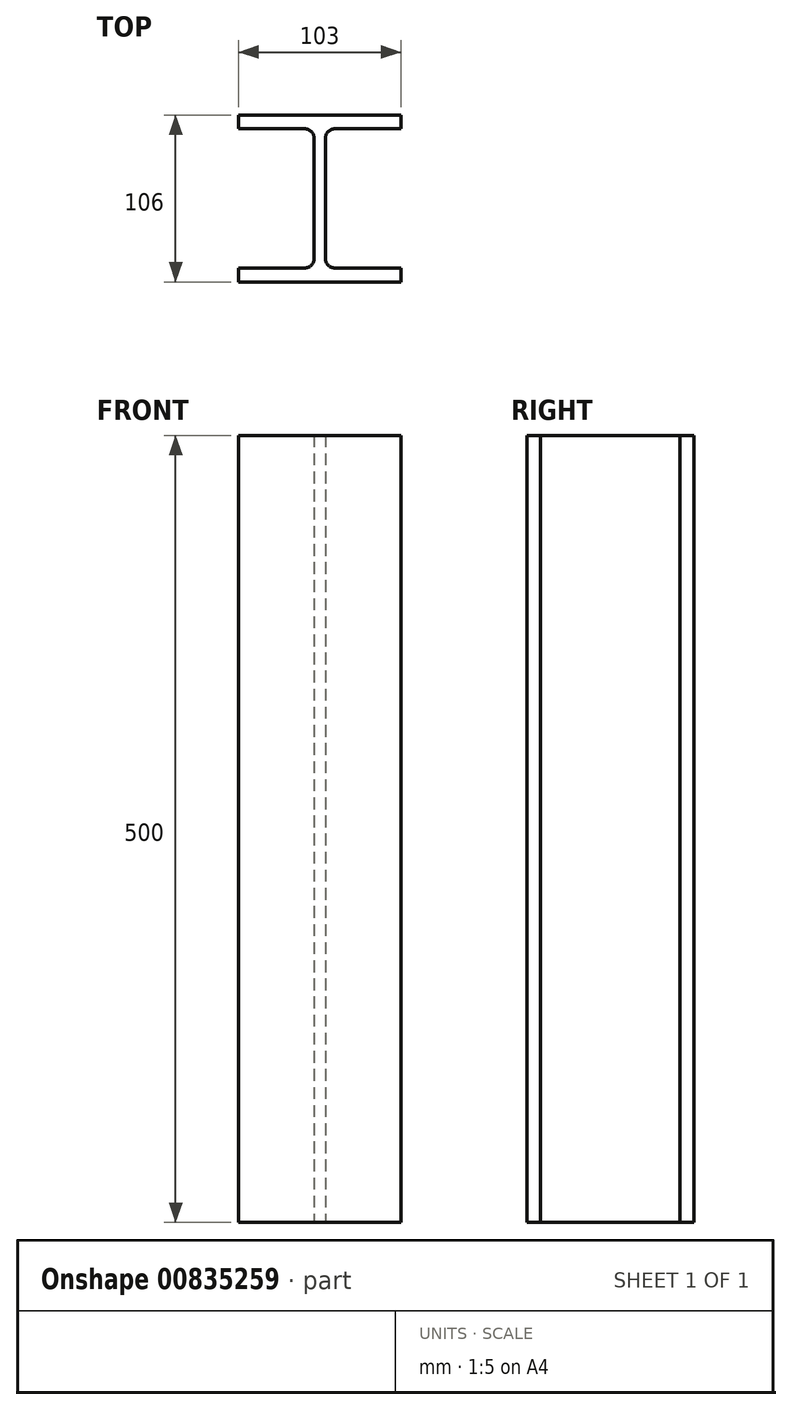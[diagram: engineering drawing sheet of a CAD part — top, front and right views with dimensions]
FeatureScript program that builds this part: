
annotation { "Feature Type Name" : "Feature", "Feature Type Description" : "" }
export const myFeature = defineFeature(function(context is Context, id is Id, definition is map)
    precondition{}
    {
        {
            var Q0;
            Q0=qCreatedBy(makeId("Top.planeOp"),FACE);
            var sketch = newSketch(context, id + "F0", { "sketchPlane" : qUnion([Q0])});
            skLineSegment(sketch, "E0.bottom", {"start": v(0, 0) * mm, "end": v(-103, 0) * mm});
            skLineSegment(sketch, "E0.top", {"start": v(0, 8.8) * mm, "end": v(-103, 8.8) * mm});
            skLineSegment(sketch, "E0.left", {"start": v(0, 0) * mm, "end": v(0, 8.8) * mm});
            skLineSegment(sketch, "E0.right", {"start": v(-103, 0) * mm, "end": v(-103, 8.8) * mm});
            skLineSegment(sketch, "E1", {"start": v(-51.5, 0) * mm, "end": v(-51.5, 106) * mm});
            skLineSegment(sketch, "E2.bottom", {"start": v(-47.95, 8.8) * mm, "end": v(-55.05, 8.8) * mm});
            skLineSegment(sketch, "E2.top", {"start": v(-47.95, 97.2) * mm, "end": v(-55.05, 97.2) * mm});
            skLineSegment(sketch, "E2.left", {"start": v(-47.95, 14.8) * mm, "end": v(-47.95, 91.2) * mm});
            skLineSegment(sketch, "E2.right", {"start": v(-55.05, 14.8) * mm, "end": v(-55.05, 91.2) * mm});
            skPoint(sketch, "E2.middle", {"position": v(-51.5, 53) * mm});
            skLineSegment(sketch, "E3", {"start": v(-51.5, 106) * mm, "end": v(0, 106) * mm});
            skLineSegment(sketch, "E4", {"start": v(0, 106) * mm, "end": v(0, 97.2) * mm});
            skLineSegment(sketch, "E5", {"start": v(0, 97.2) * mm, "end": v(-41.95, 97.2) * mm});
            skLineSegment(sketch, "E6", {"start": v(-61.05, 97.2) * mm, "end": v(-103, 97.2) * mm});
            skLineSegment(sketch, "E7", {"start": v(-103, 97.2) * mm, "end": v(-103, 106) * mm});
            skLineSegment(sketch, "E8", {"start": v(-103, 106) * mm, "end": v(-51.5, 106) * mm});
            skPoint(sketch, "E9.newPointB", {"position": v(-51.5, 97.2) * mm});
            skArc(sketch, "E9.filletArc", {"start": v(-41.95, 97.2) * mm, "mid": v(-46.2, 95.44) * mm, "end": v(-47.95, 91.2) * mm});
            skLineSegment(sketch, "E10", {"start": v(-103, 8.8) * mm, "end": v(-61.05, 8.8) * mm});
            skLineSegment(sketch, "E11", {"start": v(0, 8.8) * mm, "end": v(-41.95, 8.8) * mm});
            skPoint(sketch, "E12.visualSharp", {"position": v(-47.95, 8.8) * mm});
            skArc(sketch, "E12.filletArc", {"start": v(-47.95, 14.8) * mm, "mid": v(-46.2, 10.56) * mm, "end": v(-41.95, 8.8) * mm});
            skPoint(sketch, "E13.visualSharp", {"position": v(-55.05, 8.8) * mm});
            skArc(sketch, "E13.filletArc", {"start": v(-61.05, 8.8) * mm, "mid": v(-56.8, 10.56) * mm, "end": v(-55.05, 14.8) * mm});
            skArc(sketch, "E14.filletArc", {"start": v(-55.05, 91.2) * mm, "mid": v(-56.8, 95.44) * mm, "end": v(-61.05, 97.2) * mm});
            skSolve(sketch);
        }
        {
            var Q0;
            Q0=makeQuery(id+"F0.imprint","IMPRINT",FACE,{"disambiguationData":[TD([[makeQuery(id+"F0.imprint","IMPRINT",EDGE,{"derivedFrom":sQuery(id+"F0.wireOp",EDGE,"E2.right")}),-1.0]])]});
            var Q1;
            Q1=makeQuery(id+"F0.imprint","IMPRINT",FACE,{"disambiguationData":[TD([[makeQuery(id+"F0.imprint","IMPRINT",EDGE,{"derivedFrom":sQuery(id+"F0.wireOp",EDGE,"E2.left")}),1.0]])]});
            var Q2;
            {var subQ5=sQuery(id+"F0.wireOp",EDGE,"E0.left");Q2=makeQuery(id+"F0.imprint","IMPRINT",FACE,{"disambiguationData":[TD([[makeQuery(id+"F0.imprint","IMPRINT",EDGE,{"derivedFrom":subQ5}),1.0]])]});}
            var Q3;
            {var subQ0=sQuery(id+"F0.wireOp",EDGE,"E0.right");Q3=makeQuery(id+"F0.imprint","IMPRINT",FACE,{"disambiguationData":[TD([[makeQuery(id+"F0.imprint","IMPRINT",EDGE,{"derivedFrom":subQ0}),-1.0]])]});}
            extrude(context, id + "F1", {"entities" : qUnion([Q0, Q1, Q2, Q3]), "depth" : 500 * mm, "offsetDistance" : 25 * mm});
        }
    });
